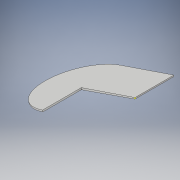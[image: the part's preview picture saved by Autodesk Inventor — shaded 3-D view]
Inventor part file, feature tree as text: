
AUTODESK INVENTOR PART (.ipt)
format: ipt  version: 2017 (Build 210142000, 142)  size: 104,960 bytes
history: native  units: in
note: dims shown in document units (in); Inventor stores cm internally (conversion verified against a paired STEP export)
features: sketch x3, extrude x2
ambient origin geometry x8: Origin, YZ Plane, XZ Plane, XY Plane, X Axis, Y Axis, Z Axis, Center Point
bodies: Solid1 (feature_tree)
feature tree (5):
  extrude  "Extrusion1"  Depth=27.2in
  extrude  "Extrusion2"  [1 undecoded]
  sketch  "Sketch4"
  sketch  "Sketch1"  dims[d2=27.2in d3=0.0in d4=27.2in]
  sketch  "Sketch3"  dims[d5=1.0in d6=0.0in]
note: 1 required parameter value undecoded (feature->parameter linkage not recoverable at this tier; creation-order binding heuristic only, values carry confidence <= 0.55)
